# Revit family: CLASSIC_DUO_700x1700x430
name_source: partatom
category: Plumbing Fixtures
units: mm (PartAtom-declared; Revit-internal decimal feet)

## family parameters
Always vertical = Yes
Cut with Voids When Loaded = No
Part Type = Normal
Room Calculation Point = No
Round Connector Dimension = Use Diameter
Shared = No
Work Plane-Based = No

## types (1)
- CLASSIC_DUO_700x1700x430
    Accessoire = Yes
    Chrome = Chrome
    Color = https://www.kaldewei.co.uk
    ColourOptions = https://www.kaldewei.co.uk
    ConnectingDimensions = EN 232
    Default Elevation = 0 mm  [stored 0 ft]
    DrainSize = 52 mm
    Durability = https://www.kaldewei.de
    Features = https://www.kaldewei.co.uk
    Finish = https://www.kaldewei.co.uk
    Finition = Kaldewei
    HasGrabHandles = https://www.kaldewei.co.uk
    IfcExportAs = BATH
    IfcExportType = IfcSanitaryTerminalType
    IntegralAccessories = https://www.kaldewei.co.uk
    Manufacturer = Kaldewei
    ManufacturerCountry = GERMANY
    ManufacturerName = KALDEWEI
    ManufacturerURL = https://www.kaldewei.com
    Material = steel enamel
    Model = CLASSIC DUO
    Name = CLASSIC DUO
    NominalDepth = 430
    NominalHeight = 565-600 mm
    NominalLength = 1700
    NominalWidth = 700
    ObjectName = CLASSIC DUO 700x1700x430
    ObjectNorm = EN 14516EU DECLARATION OF PERFORMANCE(https://www.kaldewei.de
    ObjectPicture = https://www.kaldewei.co.uk
    ObjectURL = https://www.kaldewei.co.uk
    Polantis code = KDW010002
    ProductInformation = Model No.105: The CLASSIC DUO baths radiate timeless and harmonious design. As reduced as necessary, as comfortable as possible. The inner shape of these baths extends an invitation to two people to take a seat and enjoy the comfort of two identical backrests.
    Revision = 1
    SerialNumber = 105
    Shape = Rectangular baths
    Size = 700x1700x430
    SupportFrame = https://www.kaldewei.co.uk
    Sustainability = https://kaldewei-fa.secure.footprint.net
    TechnicalDataURL = https://kaldewei.typo-live.web-factory.de
    Type Comments = CLASSIC DUO 105 700x1700x430
    UNSPSCCode = 30181500
    UNSPSCNames = Sanitary ware
    URL = https://www.kaldewei.co.uk
    Uniclass 2015 = Pr_40_20_06_08
    Version = 5
    VolumeToOverflowMaximum = 110
    WarrantyDurationParts = 30
    WarrantyDurationUnit = Year
    WarrantyStartDate = https://www.kaldewei.co.uk
    WaterSupplyOverflowAndWasteHolesOverflow = 52 mm
    WaterSupplyOverflowAndWasteHolesWaste = 52 mm
    Weight = 47

note: [stored X ft] marks values corroborated as IEEE doubles in the binary element streams (Revit-internal decimal feet)

## geometry (parser evidence)
native form markers: Sweep x12
no freeform markers — native parametric forms only
